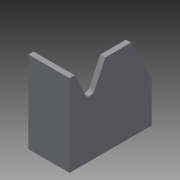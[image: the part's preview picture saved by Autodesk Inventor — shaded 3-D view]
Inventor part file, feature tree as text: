
AUTODESK INVENTOR PART (.ipt)
format: ipt  version: 2015 (Build 190159000, 159)  size: 96,256 bytes
history: native  units: in
note: dims shown in document units (in); Inventor stores cm internally (conversion verified against a paired STEP export)
features: sketch x5, other x3
ambient origin geometry x8: Origin, YZ Plane, XZ Plane, XY Plane, X Axis, Y Axis, Z Axis, Center Point
bodies: Solid1 (feature_tree)
feature tree (8):
  other  "front tab 2x2.ipt"
  other  "Solid1::front tab 2x2.ipt"
  other  "TaggingFeature1"
  sketch  "Sketch1"  dims[d0=0.3937in]
  sketch  "Sketch2"
  sketch  "Sketch3"
  sketch  "Sketch4"
  sketch  "Sketch5"
